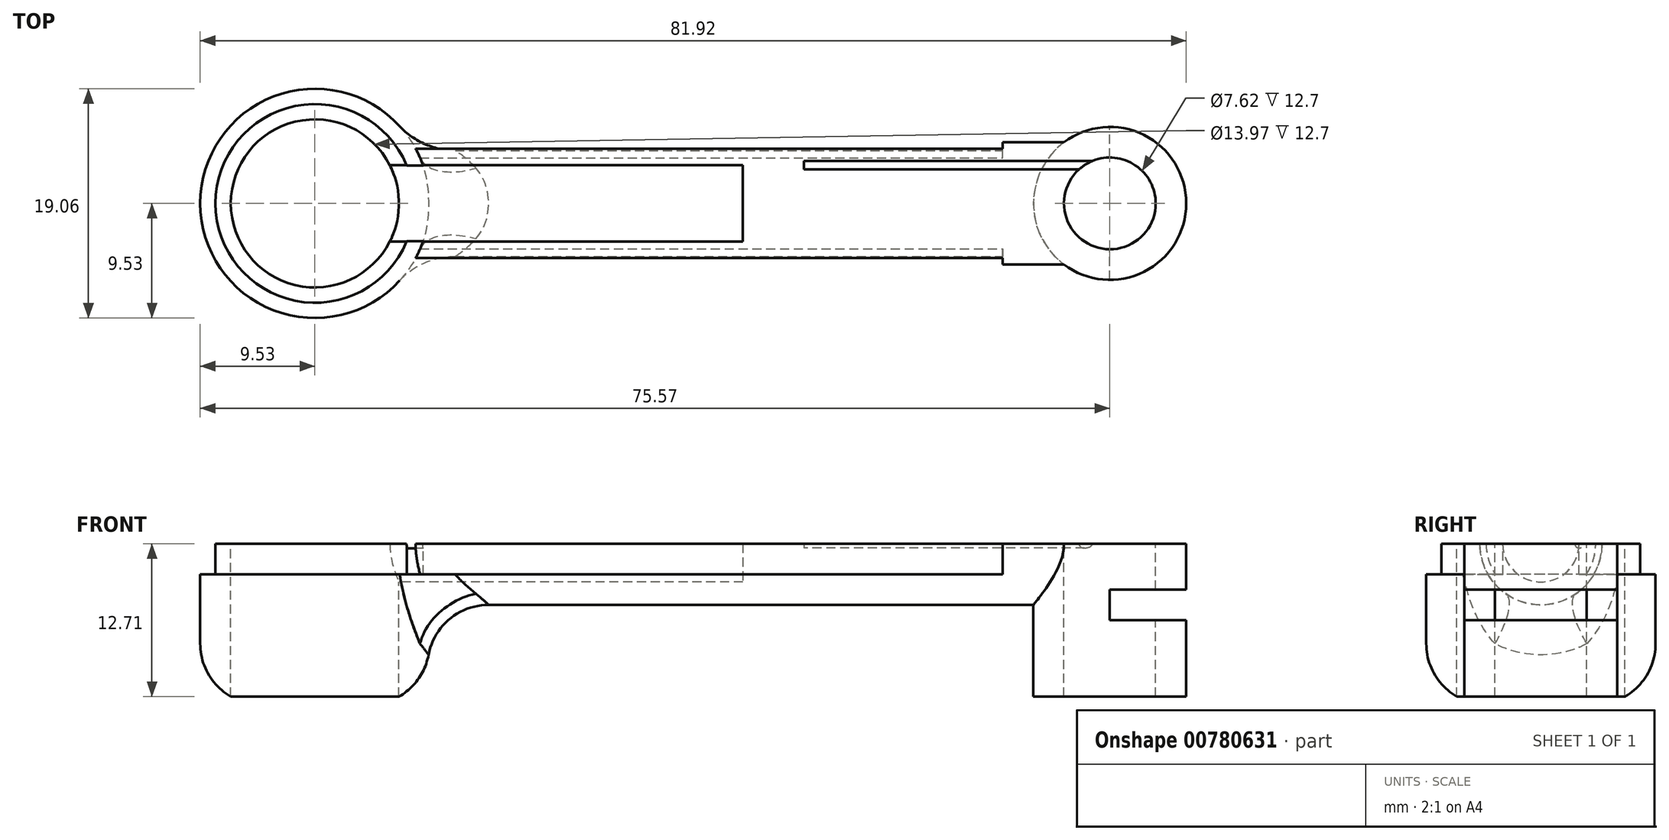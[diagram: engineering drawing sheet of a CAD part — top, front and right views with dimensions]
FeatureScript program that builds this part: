
annotation { "Feature Type Name" : "Feature", "Feature Type Description" : "" }
export const myFeature = defineFeature(function(context is Context, id is Id, definition is map)
    precondition{}
    {
        {
            var Q0;
            Q0=qCreatedBy(makeId("Top.planeOp"),FACE);
            var sketch = newSketch(context, id + "F0", { "sketchPlane" : qUnion([Q0])});
            skCircle(sketch, "E0", {"center": v(0, 0) * mm, "radius": 9.53 * mm});
            skSolve(sketch);
        }
        {
            var Q0;
            Q0=makeQuery(id+"F0.imprint","IMPRINT",FACE,{"disambiguationData":[TD([[makeQuery(id+"F0.imprint","IMPRINT",EDGE,{"derivedFrom":sQuery(id+"F0.wireOp",EDGE,"E0")}),1.0]])]});
            extrude(context, id + "F1", {"entities" : qUnion([Q0]), "depth" : 25.4 * mm, "offsetDistance" : 25.4 * mm});
        }
        {
            var Q0;
            Q0=makeQuery(id+"F1.opExtrude","CAP_FACE",FACE,{"disambiguationData":[OSD([sQuery(id+"F0.wireOp",EDGE,"E0")])],"isStart":false});
            var sketch = newSketch(context, id + "F2", { "sketchPlane" : qUnion([Q0])});
            skCircle(sketch, "E1", {"center": v(0, 0) * mm, "radius": 6.99 * mm});
            skSolve(sketch);
        }
        {
            var Q0;
            Q0=qCreatedBy(makeId("Right.planeOp"),FACE);
            var sketch = newSketch(context, id + "F3", { "sketchPlane" : qUnion([Q0])});
            skCircle(sketch, "E2", {"center": v(0, 15.88) * mm, "radius": 3.18 * mm});
            skSolve(sketch);
        }
        {
            var Q0;
            Q0=qSketchRegion(id+"F3",true);
            extrude(context, id + "F4", {"entities" : qUnion([Q0]), "operationType" : NewBodyOperationType.REMOVE, "depth" : 12.7 * mm, "offsetDistance" : 25.4 * mm});
        }
        {
            var Q0;
            Q0=qCreatedBy(makeId("Right.planeOp"),FACE);
            var sketch = newSketch(context, id + "F5", { "sketchPlane" : qUnion([Q0])});
            skLineSegment(sketch, "E3.top", {"start": v(9.53, 15.88) * mm, "end": v(-9.53, 15.88) * mm});
            skPoint(sketch, "E3.middle", {"position": v(0, 7.94) * mm});
            skLineSegment(sketch, "E4", {"start": v(-9.53, 15.88) * mm, "end": v(-9.53, 28.58) * mm});
            skLineSegment(sketch, "E5", {"start": v(9.53, 15.88) * mm, "end": v(9.53, 28.58) * mm});
            skLineSegment(sketch, "E6", {"start": v(-9.53, 28.58) * mm, "end": v(9.53, 28.58) * mm});
            skSolve(sketch);
        }
        {
            var Q0;
            Q0=qSketchRegion(id+"F5",true);
            extrude(context, id + "F6", {"entities" : qUnion([Q0]), "operationType" : NewBodyOperationType.REMOVE, "oppositeDirection" : true, "depth" : 25.4 * mm, "offsetDistance" : 25.4 * mm, "symmetric" : true});
        }
        {
            var Q0;
            Q0=qCreatedBy(makeId("Right.planeOp"),FACE);
            var sketch = newSketch(context, id + "F7", { "sketchPlane" : qUnion([Q0])});
            skArc(sketch, "E7", {"start": v(3.18, 15.88) * mm, "mid": v(0, 12.7) * mm, "end": v(-3.18, 15.88) * mm});
            skArc(sketch, "E8", {"start": v(-3.15, 18.42) * mm, "mid": v(-3.82, 17.22) * mm, "end": v(-4.05, 15.88) * mm});
            skArc(sketch, "E9", {"start": v(3.15, 18.42) * mm, "mid": v(3.82, 17.22) * mm, "end": v(4.05, 15.88) * mm});
            skLineSegment(sketch, "E10", {"start": v(-3.15, 18.42) * mm, "end": v(-4.4, 18.42) * mm});
            skLineSegment(sketch, "E11", {"start": v(3.15, 18.42) * mm, "end": v(4.4, 18.42) * mm});
            skLineSegment(sketch, "E12", {"start": v(-3.18, 15.88) * mm, "end": v(-4.05, 15.88) * mm});
            skLineSegment(sketch, "E13", {"start": v(3.18, 15.88) * mm, "end": v(4.05, 15.88) * mm});
            skArc(sketch, "E14", {"start": v(-4.4, 18.42) * mm, "mid": v(0, 10.8) * mm, "end": v(4.4, 18.42) * mm});
            skSolve(sketch);
        }
        {
            var Q0;
            Q0=qSketchRegion(id+"F7",true);
            var Q1;
            Q1=qConstructionFilter(qBodyType(qCreatedBy(id+"F7",EDGE),BodyType.WIRE),ConstructionObject.NO);
            extrude(context, id + "F8", {"entities" : qUnion([Q0]), "operationType" : NewBodyOperationType.ADD, "surfaceEntities" : qUnion([Q1]), "depth" : 38.1 * mm, "offsetDistance" : 25.4 * mm});
        }
        {
            var Q0;
            Q0=makeQuery(id+"F2.imprint","IMPRINT",FACE,{"disambiguationData":[TD([[makeQuery(id+"F2.imprint","IMPRINT",EDGE,{"derivedFrom":sQuery(id+"F2.wireOp",EDGE,"E1")}),1.0]])]});
            extrude(context, id + "F9", {"entities" : qUnion([Q0]), "operationType" : NewBodyOperationType.REMOVE, "oppositeDirection" : true, "depth" : 12.7 * mm, "offsetDistance" : 25.4 * mm});
        }
        {
            var Q0;
            Q0=makeQuery(id+"F8.opExtrude","CAP_FACE",FACE,{"disambiguationData":[OSD([sQuery(id+"F7.wireOp",EDGE,"E7"),sQuery(id+"F7.wireOp",EDGE,"E8"),sQuery(id+"F7.wireOp",EDGE,"E9"),sQuery(id+"F7.wireOp",EDGE,"E10"),sQuery(id+"F7.wireOp",EDGE,"E11"),sQuery(id+"F7.wireOp",EDGE,"E12"),sQuery(id+"F7.wireOp",EDGE,"E13"),sQuery(id+"F7.wireOp",EDGE,"E14")])],"isStart":false});
            var sketch = newSketch(context, id + "F10", { "sketchPlane" : qUnion([Q0])});
            skArc(sketch, "E15", {"start": v(-5.08, 15.88) * mm, "mid": v(0, 10.8) * mm, "end": v(5.08, 15.88) * mm});
            skArc(sketch, "E16", {"start": v(3.53, 15.88) * mm, "mid": v(3.17, 15.52) * mm, "end": v(2.82, 15.88) * mm});
            skLineSegment(sketch, "E17", {"start": v(-5.08, 15.88) * mm, "end": v(2.82, 15.88) * mm});
            skLineSegment(sketch, "E18", {"start": v(3.53, 15.88) * mm, "end": v(5.08, 15.88) * mm});
            skSolve(sketch);
        }
        {
            var Q0;
            Q0=qSketchRegion(id+"F10",true);
            extrude(context, id + "F11", {"entities" : qUnion([Q0]), "operationType" : NewBodyOperationType.ADD, "depth" : 24.13 * mm, "offsetDistance" : 25.4 * mm});
        }
        {
            var Q0;
            Q0=makeQuery(id+"F1.opExtrude","CAP_FACE",FACE,{"disambiguationData":[OSD([sQuery(id+"F0.wireOp",EDGE,"E0")])],"isStart":true});
            var sketch = newSketch(context, id + "F12", { "sketchPlane" : qUnion([Q0])});
            skCircle(sketch, "E19", {"center": v(-3.18, 3.18) * mm, "radius": 0.95 * mm});
            skCircle(sketch, "E20", {"center": v(3.18, 3.18) * mm, "radius": 0.95 * mm});
            skCircle(sketch, "E21", {"center": v(3.18, -3.18) * mm, "radius": 0.95 * mm});
            skCircle(sketch, "E22", {"center": v(-3.18, -3.18) * mm, "radius": 0.95 * mm});
            skSolve(sketch);
        }
        {
            var Q0;
            Q0=qSketchRegion(id+"F12",true);
            extrude(context, id + "F13", {"entities" : qUnion([Q0]), "operationType" : NewBodyOperationType.REMOVE, "oppositeDirection" : true, "depth" : 25.4 * mm, "offsetDistance" : 25.4 * mm});
        }
        {
            var Q0;
            Q0=makeQuery(id+"F1.opExtrude","CAP_FACE",FACE,{"disambiguationData":[OSD([sQuery(id+"F0.wireOp",EDGE,"E0")])],"isStart":true});
            var sketch = newSketch(context, id + "F14", { "sketchPlane" : qUnion([Q0])});
            skCircle(sketch, "E23", {"center": v(0, 0) * mm, "radius": 6.99 * mm});
            skSolve(sketch);
        }
        {
            var Q0;
            Q0=qSketchRegion(id+"F14",true);
            extrude(context, id + "F15", {"entities" : qUnion([Q0]), "operationType" : NewBodyOperationType.REMOVE, "oppositeDirection" : true, "depth" : 7.62 * mm, "offsetDistance" : 25.4 * mm});
        }
        {
            var Q0;
            Q0=makeQuery(id+"F9.boolean.opBoolean","SPLIT",FACE,{"disambiguationData":[TD([makeQuery(id+"F1.opExtrude","SWEPT_FACE",FACE,{"disambiguationData":[OSD([sQuery(id+"F0.wireOp",EDGE,"E0")])]})])],"derivedFrom":makeQuery(id+"F8.boolean.opBoolean","MERGE",FACE,{"derivedFrom":[makeQuery(id+"F6.boolean.opBoolean","COPY",FACE,{"derivedFrom":makeQuery(id+"F6.opExtrude","SWEPT_FACE",FACE,{"disambiguationData":[OSD([sQuery(id+"F5.wireOp",EDGE,"E3.top")])]})}),makeQuery(id+"F8.opExtrude","SWEPT_FACE",FACE,{"disambiguationData":[OSD([sQuery(id+"F7.wireOp",EDGE,"E12")])]}),makeQuery(id+"F8.opExtrude","SWEPT_FACE",FACE,{"disambiguationData":[OSD([sQuery(id+"F7.wireOp",EDGE,"E13")])]})]})});
            var sketch = newSketch(context, id + "F16", { "sketchPlane" : qUnion([Q0])});
            skCircle(sketch, "E24", {"center": v(0, 0) * mm, "radius": 6.99 * mm});
            skCircle(sketch, "E25", {"center": v(0, 0) * mm, "radius": 8.26 * mm});
            skSolve(sketch);
        }
        {
            var Q0;
            Q0=qSketchRegion(id+"F16",true);
            extrude(context, id + "F17", {"entities" : qUnion([Q0]), "operationType" : NewBodyOperationType.REMOVE, "depth" : 25.4 * mm, "offsetDistance" : 25.4 * mm});
        }
        {
            var Q0;
            Q0=makeQuery(id+"F8.opExtrude","SWEPT_FACE",FACE,{"disambiguationData":[OSD([sQuery(id+"F7.wireOp",EDGE,"E11")])]});
            var sketch = newSketch(context, id + "F18", { "sketchPlane" : qUnion([Q0])});
            skArc(sketch, "E26", {"start": v(7.63, 3.15) * mm, "mid": v(-8.25, 0) * mm, "end": v(7.63, -3.15) * mm});
            skArc(sketch, "E27", {"start": v(8.99, 3.15) * mm, "mid": v(-9.53, 0) * mm, "end": v(8.99, -3.15) * mm});
            skLineSegment(sketch, "E28", {"start": v(7.63, 3.15) * mm, "end": v(8.99, 3.15) * mm});
            skLineSegment(sketch, "E29", {"start": v(7.63, -3.15) * mm, "end": v(8.99, -3.15) * mm});
            skSolve(sketch);
        }
        {
            var Q0;
            Q0=qSketchRegion(id+"F18",true);
            extrude(context, id + "F19", {"entities" : qUnion([Q0]), "operationType" : NewBodyOperationType.REMOVE, "oppositeDirection" : true, "depth" : 5.08 * mm, "offsetDistance" : 25.4 * mm});
        }
        {
            var Q0;
            {var subQ0=sQuery(id+"F7.wireOp",EDGE,"E10");var subQ1=sQuery(id+"F7.wireOp",EDGE,"E8");var subQ2=sQuery(id+"F7.wireOp",EDGE,"E12");var subQ3=sQuery(id+"F7.wireOp",EDGE,"E13");var subQ4=sQuery(id+"F7.wireOp",EDGE,"E14");Q0=makeQuery(id+"F11.boolean.opBoolean","SPLIT",FACE,{"disambiguationData":[TD([makeQuery(id+"F8.opExtrude","SWEPT_FACE",FACE,{"disambiguationData":[OSD([subQ1])]})])],"derivedFrom":makeQuery(id+"F8.opExtrude","CAP_FACE",FACE,{"disambiguationData":[OSD([sQuery(id+"F7.wireOp",EDGE,"E7"),subQ1,sQuery(id+"F7.wireOp",EDGE,"E9"),subQ0,sQuery(id+"F7.wireOp",EDGE,"E11"),subQ2,subQ3,subQ4])],"isStart":false})});}
            var sketch = newSketch(context, id + "F20", { "sketchPlane" : qUnion([Q0])});
            skArc(sketch, "E30", {"start": v(-4.05, 15.88) * mm, "mid": v(0, 19.92) * mm, "end": v(4.05, 15.88) * mm});
            skLineSegment(sketch, "E31", {"start": v(-4.05, 15.88) * mm, "end": v(4.05, 15.88) * mm});
            skSolve(sketch);
        }
        {
            var Q0;
            Q0=qSketchRegion(id+"F20",true);
            extrude(context, id + "F21", {"entities" : qUnion([Q0]), "operationType" : NewBodyOperationType.REMOVE, "oppositeDirection" : true, "depth" : 63.5 * mm, "offsetDistance" : 25.4 * mm});
        }
        {
            var Q0;
            {var subQ0=sQuery(id+"F7.wireOp",EDGE,"E10");var subQ1=sQuery(id+"F7.wireOp",EDGE,"E8");var subQ2=sQuery(id+"F7.wireOp",EDGE,"E12");var subQ3=sQuery(id+"F7.wireOp",EDGE,"E13");var subQ4=sQuery(id+"F7.wireOp",EDGE,"E14");Q0=makeQuery(id+"F11.boolean.opBoolean","SPLIT",FACE,{"disambiguationData":[TD([makeQuery(id+"F8.opExtrude","SWEPT_FACE",FACE,{"disambiguationData":[OSD([subQ1])]})])],"derivedFrom":makeQuery(id+"F8.opExtrude","CAP_FACE",FACE,{"disambiguationData":[OSD([sQuery(id+"F7.wireOp",EDGE,"E7"),subQ1,sQuery(id+"F7.wireOp",EDGE,"E9"),subQ0,sQuery(id+"F7.wireOp",EDGE,"E11"),subQ2,subQ3,subQ4])],"isStart":false})});}
            var sketch = newSketch(context, id + "F22", { "sketchPlane" : qUnion([Q0])});
            skArc(sketch, "E32", {"start": v(-3.78, 13.34) * mm, "mid": v(-4.35, 14.55) * mm, "end": v(-4.55, 15.88) * mm});
            skLineSegment(sketch, "E33", {"start": v(-3.78, 13.34) * mm, "end": v(-4.4, 13.34) * mm});
            skArc(sketch, "E34", {"start": v(-3.15, 18.42) * mm, "mid": v(-3.82, 17.22) * mm, "end": v(-4.05, 15.88) * mm});
            skLineSegment(sketch, "E35", {"start": v(-4.55, 15.88) * mm, "end": v(-4.05, 15.88) * mm});
            skLineSegment(sketch, "E36", {"start": v(-3.15, 18.42) * mm, "end": v(-4.4, 18.42) * mm});
            skArc(sketch, "E37", {"start": v(-4.4, 13.34) * mm, "mid": v(-5.08, 15.88) * mm, "end": v(-4.4, 18.42) * mm});
            skSolve(sketch);
        }
        {
            var Q0;
            Q0=qSketchRegion(id+"F22",true);
            extrude(context, id + "F23", {"entities" : qUnion([Q0]), "operationType" : NewBodyOperationType.REMOVE, "oppositeDirection" : true, "depth" : 30.48 * mm, "offsetDistance" : 25.4 * mm});
        }
        {
            var Q0;
            {var subQ0=sQuery(id+"F7.wireOp",EDGE,"E11");var subQ1=sQuery(id+"F7.wireOp",EDGE,"E9");var subQ2=sQuery(id+"F7.wireOp",EDGE,"E12");var subQ3=sQuery(id+"F7.wireOp",EDGE,"E13");var subQ4=sQuery(id+"F7.wireOp",EDGE,"E14");Q0=makeQuery(id+"F11.boolean.opBoolean","SPLIT",FACE,{"disambiguationData":[TD([makeQuery(id+"F8.opExtrude","SWEPT_FACE",FACE,{"disambiguationData":[OSD([subQ1])]})])],"derivedFrom":makeQuery(id+"F8.opExtrude","CAP_FACE",FACE,{"disambiguationData":[OSD([sQuery(id+"F7.wireOp",EDGE,"E7"),sQuery(id+"F7.wireOp",EDGE,"E8"),subQ1,sQuery(id+"F7.wireOp",EDGE,"E10"),subQ0,subQ2,subQ3,subQ4])],"isStart":false})});}
            var sketch = newSketch(context, id + "F24", { "sketchPlane" : qUnion([Q0])});
            skArc(sketch, "E38", {"start": v(3.78, 13.34) * mm, "mid": v(4.35, 14.55) * mm, "end": v(4.55, 15.88) * mm});
            skLineSegment(sketch, "E39", {"start": v(4.55, 15.88) * mm, "end": v(4.05, 15.88) * mm});
            skArc(sketch, "E40", {"start": v(4.05, 15.88) * mm, "mid": v(3.82, 17.22) * mm, "end": v(3.15, 18.42) * mm});
            skLineSegment(sketch, "E41", {"start": v(3.15, 18.42) * mm, "end": v(4.4, 18.42) * mm});
            skLineSegment(sketch, "E42", {"start": v(3.78, 13.34) * mm, "end": v(4.4, 13.34) * mm});
            skArc(sketch, "E43", {"start": v(4.4, 13.34) * mm, "mid": v(5.08, 15.88) * mm, "end": v(4.4, 18.42) * mm});
            skSolve(sketch);
        }
        {
            var Q0;
            Q0=qSketchRegion(id+"F24",true);
            extrude(context, id + "F25", {"entities" : qUnion([Q0]), "operationType" : NewBodyOperationType.REMOVE, "oppositeDirection" : true, "depth" : 30.48 * mm, "offsetDistance" : 25.4 * mm});
        }
        {
            var Q0;
            Q0=qCreatedBy(makeId("Right.planeOp"),FACE);
            var sketch = newSketch(context, id + "F26", { "sketchPlane" : qUnion([Q0])});
            skLineSegment(sketch, "E44.bottom", {"start": v(-9.53, 0) * mm, "end": v(9.53, 0) * mm});
            skLineSegment(sketch, "E44.top", {"start": v(-9.53, 3.17) * mm, "end": v(9.53, 3.17) * mm});
            skLineSegment(sketch, "E44.left", {"start": v(-9.53, 0) * mm, "end": v(-9.53, 3.17) * mm});
            skLineSegment(sketch, "E44.right", {"start": v(9.53, 0) * mm, "end": v(9.53, 3.17) * mm});
            skSolve(sketch);
        }
        {
            var Q0;
            Q0=qSketchRegion(id+"F26",true);
            extrude(context, id + "F27", {"entities" : qUnion([Q0]), "operationType" : NewBodyOperationType.REMOVE, "oppositeDirection" : true, "depth" : 25.4 * mm, "offsetDistance" : 25.4 * mm, "symmetric" : true});
        }
        {
            var Q0;
            Q0=makeQuery(id+"F15.boolean.opBoolean","COPY",FACE,{"derivedFrom":makeQuery(id+"F15.opExtrude","CAP_FACE",FACE,{"disambiguationData":[OSD([sQuery(id+"F14.wireOp",EDGE,"E23")])],"isStart":false})});
            var sketch = newSketch(context, id + "F28", { "sketchPlane" : qUnion([Q0])});
            skCircle(sketch, "E45", {"center": v(0, 0) * mm, "radius": 6.99 * mm});
            skSolve(sketch);
        }
        {
            var Q0;
            Q0=qSketchRegion(id+"F28",true);
            extrude(context, id + "F29", {"entities" : qUnion([Q0]), "operationType" : NewBodyOperationType.REMOVE, "oppositeDirection" : true, "depth" : 25.4 * mm, "offsetDistance" : 25.4 * mm});
        }
        {
            var Q0;
            Q0=makeQuery(id+"F27.boolean.opBoolean","INTERSECT",EDGE,{"derivedFrom":[makeQuery(id+"F1.opExtrude","SWEPT_FACE",FACE,{"disambiguationData":[OSD([sQuery(id+"F0.wireOp",EDGE,"E0")])]}),makeQuery(id+"F27.opExtrude","SWEPT_FACE",FACE,{"disambiguationData":[OSD([sQuery(id+"F26.wireOp",EDGE,"E44.top")])]})]});
            fillet(context, id + "F30", {"entities" : qUnion([Q0]), "radius" : 5.08 * mm, "tangentPropagation" : true, "allowEdgeOverflow" : false});
        }
        {
            var Q0;
            Q0=makeQuery(id+"F19.boolean.opBoolean","SPLIT",EDGE,{"derivedFrom":makeQuery(id+"F8.boolean.opBoolean","INTERSECT",EDGE,{"derivedFrom":[makeQuery(id+"F1.opExtrude","SWEPT_FACE",FACE,{"disambiguationData":[OSD([sQuery(id+"F0.wireOp",EDGE,"E0")])]}),makeQuery(id+"F8.opExtrude","SWEPT_FACE",FACE,{"disambiguationData":[OSD([sQuery(id+"F7.wireOp",EDGE,"E14")])]})]})});
            fillet(context, id + "F31", {"entities" : qUnion([Q0]), "radius" : 5.08 * mm, "tangentPropagation" : true, "allowEdgeOverflow" : false});
        }
        {
            var Q0;
            {var subQ0=sQuery(id+"F7.wireOp",EDGE,"E9");var subQ1=makeQuery(id+"F8.opExtrude","SWEPT_FACE",FACE,{"disambiguationData":[OSD([subQ0])]});var subQ2=sQuery(id+"F10.wireOp",EDGE,"aL0u9GlF-6Q7s-W1V7-4wS0-8lCQG8VcdnJv");var subQ3=sQuery(id+"F10.wireOp",EDGE,"2Tc0jqr0-cNR8-OvJQ-WwAY-mDO75ud9QsQn");var subQ7=sQuery(id+"F7.wireOp",EDGE,"E13");var subQ8=sQuery(id+"F7.wireOp",EDGE,"E12");var subQ9=sQuery(id+"F7.wireOp",EDGE,"E8");var subQ16=makeQuery(id+"F8.boolean.opBoolean","MERGE",FACE,{"derivedFrom":[makeQuery(id+"F6.boolean.opBoolean","COPY",FACE,{"derivedFrom":makeQuery(id+"F6.opExtrude","SWEPT_FACE",FACE,{"disambiguationData":[OSD([sQuery(id+"F5.wireOp",EDGE,"E3.top")])]})}),makeQuery(id+"F8.opExtrude","SWEPT_FACE",FACE,{"disambiguationData":[OSD([subQ8])]}),makeQuery(id+"F8.opExtrude","SWEPT_FACE",FACE,{"disambiguationData":[OSD([subQ7])]})]});Q0=makeQuery(id+"F25.boolean.opBoolean","MERGE",FACE,{"derivedFrom":[makeQuery(id+"F19.boolean.opBoolean","SPLIT",FACE,{"disambiguationData":[TD([subQ1])],"derivedFrom":makeQuery(id+"F17.boolean.opBoolean","MERGE",FACE,{"derivedFrom":[makeQuery(id+"F9.boolean.opBoolean","SPLIT",FACE,{"disambiguationData":[TD([makeQuery(id+"F1.opExtrude","SWEPT_FACE",FACE,{"disambiguationData":[OSD([sQuery(id+"F0.wireOp",EDGE,"E0")])]})])],"derivedFrom":subQ16}),makeQuery(id+"F11.boolean.opBoolean","MERGE",FACE,{"derivedFrom":[makeQuery(id+"F9.boolean.opBoolean","SPLIT",FACE,{"disambiguationData":[TD([makeQuery(id+"F8.opExtrude","SWEPT_FACE",FACE,{"disambiguationData":[OSD([subQ9])]})])],"derivedFrom":subQ16}),makeQuery(id+"F11.opExtrude","SWEPT_FACE",FACE,{"disambiguationData":[OSD([subQ2])]})]}),makeQuery(id+"F11.boolean.opBoolean","MERGE",FACE,{"derivedFrom":[makeQuery(id+"F9.boolean.opBoolean","SPLIT",FACE,{"disambiguationData":[TD([subQ1])],"derivedFrom":subQ16}),makeQuery(id+"F11.opExtrude","SWEPT_FACE",FACE,{"disambiguationData":[OSD([subQ3])]})]}),makeQuery(id+"F17.opExtrude","CAP_FACE",FACE,{"disambiguationData":[OSD([sQuery(id+"F16.wireOp",EDGE,"E24"),sQuery(id+"F16.wireOp",EDGE,"E25")])],"isStart":true})]})}),makeQuery(id+"F25.opExtrude","SWEPT_FACE",FACE,{"disambiguationData":[OSD([sQuery(id+"F24.wireOp",EDGE,"E39")])]})]});}
            var sketch = newSketch(context, id + "F32", { "sketchPlane" : qUnion([Q0])});
            skCircle(sketch, "E46", {"center": v(66.04, 0) * mm, "radius": 3.81 * mm});
            skCircle(sketch, "E47", {"center": v(66.04, 0) * mm, "radius": 6.35 * mm});
            skSolve(sketch);
        }
        {
            var Q0;
            Q0=qSketchRegion(id+"F32",true);
            extrude(context, id + "F33", {"entities" : qUnion([Q0]), "operationType" : NewBodyOperationType.ADD, "oppositeDirection" : true, "depth" : 12.7 * mm, "offsetDistance" : 25.4 * mm});
        }
        {
            var Q0;
            Q0=makeQuery(id+"F11.opExtrude","CAP_FACE",FACE,{"disambiguationData":[OSD([sQuery(id+"F10.wireOp",EDGE,"E15"),sQuery(id+"F10.wireOp",EDGE,"00xkIltH-ur7c-vDCf-NMd2-okXEgH0ywGPR"),sQuery(id+"F10.wireOp",EDGE,"2Tc0jqr0-cNR8-OvJQ-WwAY-mDO75ud9QsQn"),sQuery(id+"F10.wireOp",EDGE,"aL0u9GlF-6Q7s-W1V7-4wS0-8lCQG8VcdnJv")])],"isStart":true});
            var sketch = newSketch(context, id + "F34", { "sketchPlane" : qUnion([Q0])});
            skArc(sketch, "E48", {"start": v(-3.18, 15.88) * mm, "mid": v(0, 12.7) * mm, "end": v(3.18, 15.88) * mm});
            skLineSegment(sketch, "E49", {"start": v(-3.18, 15.88) * mm, "end": v(3.18, 15.88) * mm});
            skSolve(sketch);
        }
        {
            var Q0;
            Q0=qSketchRegion(id+"F34",true);
            extrude(context, id + "F35", {"entities" : qUnion([Q0]), "operationType" : NewBodyOperationType.ADD, "depth" : 2.54 * mm, "offsetDistance" : 25.4 * mm});
        }
        {
            var Q0;
            {var subQ0=sQuery(id+"F7.wireOp",EDGE,"E7");var subQ1=sQuery(id+"F7.wireOp",EDGE,"E12");var subQ4=sQuery(id+"F7.wireOp",EDGE,"E13");Q0=makeQuery(id+"F35.boolean.opBoolean","MERGE",FACE,{"derivedFrom":[makeQuery(id+"F11.boolean.opBoolean","SPLIT",FACE,{"disambiguationData":[TD([makeQuery(id+"F4.boolean.opBoolean","COPY",FACE,{"derivedFrom":makeQuery(id+"F4.opExtrude","SWEPT_FACE",FACE,{"disambiguationData":[OSD([sQuery(id+"F3.wireOp",EDGE,"E2")])]})})])],"derivedFrom":makeQuery(id+"F8.opExtrude","CAP_FACE",FACE,{"disambiguationData":[OSD([subQ0,sQuery(id+"F7.wireOp",EDGE,"E8"),sQuery(id+"F7.wireOp",EDGE,"E9"),sQuery(id+"F7.wireOp",EDGE,"E10"),sQuery(id+"F7.wireOp",EDGE,"E11"),subQ1,subQ4,sQuery(id+"F7.wireOp",EDGE,"E14")])],"isStart":false})}),makeQuery(id+"F35.opExtrude","CAP_FACE",FACE,{"disambiguationData":[OSD([sQuery(id+"F34.wireOp",EDGE,"E48"),sQuery(id+"F34.wireOp",EDGE,"E49")])],"isStart":true})]});}
            extrude(context, id + "F36", {"entities" : qUnion([Q0]), "operationType" : NewBodyOperationType.REMOVE, "depth" : 27.94 * mm, "offsetDistance" : 25.4 * mm});
        }
        {
            var Q0;
            Q0=makeQuery(id+"F23.boolean.opBoolean","COPY",FACE,{"derivedFrom":makeQuery(id+"F23.opExtrude","CAP_FACE",FACE,{"disambiguationData":[OSD([sQuery(id+"F22.wireOp",EDGE,"E32"),sQuery(id+"F22.wireOp",EDGE,"E33"),sQuery(id+"F22.wireOp",EDGE,"E34"),sQuery(id+"F22.wireOp",EDGE,"E35"),sQuery(id+"F22.wireOp",EDGE,"E36"),sQuery(id+"F22.wireOp",EDGE,"E37")])],"isStart":true})});
            extrude(context, id + "F37", {"entities" : qUnion([Q0]), "operationType" : NewBodyOperationType.REMOVE, "oppositeDirection" : true, "depth" : 19.05 * mm, "offsetDistance" : 25.4 * mm});
        }
        {
            var Q0;
            Q0=makeQuery(id+"F25.boolean.opBoolean","COPY",FACE,{"derivedFrom":makeQuery(id+"F25.opExtrude","CAP_FACE",FACE,{"disambiguationData":[OSD([sQuery(id+"F24.wireOp",EDGE,"E38"),sQuery(id+"F24.wireOp",EDGE,"E39"),sQuery(id+"F24.wireOp",EDGE,"E40"),sQuery(id+"F24.wireOp",EDGE,"E41"),sQuery(id+"F24.wireOp",EDGE,"E42"),sQuery(id+"F24.wireOp",EDGE,"E43")])],"isStart":true})});
            extrude(context, id + "F38", {"entities" : qUnion([Q0]), "operationType" : NewBodyOperationType.REMOVE, "oppositeDirection" : true, "depth" : 19.05 * mm, "offsetDistance" : 25.4 * mm});
        }
        {
            var Q0;
            {var subQ0=sQuery(id+"F7.wireOp",EDGE,"E9");var subQ1=makeQuery(id+"F8.opExtrude","SWEPT_FACE",FACE,{"disambiguationData":[OSD([subQ0])]});var subQ2=sQuery(id+"F10.wireOp",EDGE,"Va9SlXQ7-r9gY-A2W4-oZNz-J4n8oxZGjyvQ");var subQ3=sQuery(id+"F10.wireOp",EDGE,"Rd6kEXFY-NNdW-kPoJ-Zn7l-Uw842lO794nO");var subQ8=sQuery(id+"F7.wireOp",EDGE,"E13");var subQ9=sQuery(id+"F7.wireOp",EDGE,"E12");var subQ10=sQuery(id+"F7.wireOp",EDGE,"E8");var subQ20=makeQuery(id+"F8.boolean.opBoolean","MERGE",FACE,{"derivedFrom":[makeQuery(id+"F6.boolean.opBoolean","COPY",FACE,{"derivedFrom":makeQuery(id+"F6.opExtrude","SWEPT_FACE",FACE,{"disambiguationData":[OSD([sQuery(id+"F5.wireOp",EDGE,"E3.top")])]})}),makeQuery(id+"F8.opExtrude","SWEPT_FACE",FACE,{"disambiguationData":[OSD([subQ9])]}),makeQuery(id+"F8.opExtrude","SWEPT_FACE",FACE,{"disambiguationData":[OSD([subQ8])]})]});var subQ21=makeQuery(id+"F8.opExtrude","SWEPT_FACE",FACE,{"disambiguationData":[OSD([subQ10])]});var subQ22=makeQuery(id+"F17.boolean.opBoolean","MERGE",FACE,{"derivedFrom":[makeQuery(id+"F9.boolean.opBoolean","SPLIT",FACE,{"disambiguationData":[TD([makeQuery(id+"F1.opExtrude","SWEPT_FACE",FACE,{"disambiguationData":[OSD([sQuery(id+"F0.wireOp",EDGE,"E0")])]})])],"derivedFrom":subQ20}),makeQuery(id+"F11.boolean.opBoolean","MERGE",FACE,{"derivedFrom":[makeQuery(id+"F9.boolean.opBoolean","SPLIT",FACE,{"disambiguationData":[TD([subQ21])],"derivedFrom":subQ20}),makeQuery(id+"F11.opExtrude","SWEPT_FACE",FACE,{"disambiguationData":[OSD([subQ2])]})]}),makeQuery(id+"F11.boolean.opBoolean","MERGE",FACE,{"derivedFrom":[makeQuery(id+"F9.boolean.opBoolean","SPLIT",FACE,{"disambiguationData":[TD([subQ1])],"derivedFrom":subQ20}),makeQuery(id+"F11.opExtrude","SWEPT_FACE",FACE,{"disambiguationData":[OSD([subQ3])]})]}),makeQuery(id+"F17.opExtrude","CAP_FACE",FACE,{"disambiguationData":[OSD([sQuery(id+"F16.wireOp",EDGE,"E24"),sQuery(id+"F16.wireOp",EDGE,"E25")])],"isStart":true})]});Q0=makeQuery(id+"F35.boolean.opBoolean","MERGE",FACE,{"derivedFrom":[makeQuery(id+"F33.boolean.opBoolean","MERGE",FACE,{"derivedFrom":[makeQuery(id+"F23.boolean.opBoolean","MERGE",FACE,{"derivedFrom":[makeQuery(id+"F19.boolean.opBoolean","SPLIT",FACE,{"disambiguationData":[TD([subQ21])],"derivedFrom":subQ22}),makeQuery(id+"F23.opExtrude","SWEPT_FACE",FACE,{"disambiguationData":[OSD([sQuery(id+"F22.wireOp",EDGE,"E35")])]})]}),makeQuery(id+"F25.boolean.opBoolean","MERGE",FACE,{"derivedFrom":[makeQuery(id+"F19.boolean.opBoolean","SPLIT",FACE,{"disambiguationData":[TD([subQ1])],"derivedFrom":subQ22}),makeQuery(id+"F25.opExtrude","SWEPT_FACE",FACE,{"disambiguationData":[OSD([sQuery(id+"F24.wireOp",EDGE,"E39")])]})]}),makeQuery(id+"F33.opExtrude","CAP_FACE",FACE,{"disambiguationData":[OSD([sQuery(id+"F32.wireOp",EDGE,"E46"),sQuery(id+"F32.wireOp",EDGE,"E47")])],"isStart":true})]}),makeQuery(id+"F35.opExtrude","SWEPT_FACE",FACE,{"disambiguationData":[OSD([sQuery(id+"F34.wireOp",EDGE,"E49")])]})]});}
            var sketch = newSketch(context, id + "F39", { "sketchPlane" : qUnion([Q0])});
            skArc(sketch, "E50", {"start": v(66.04, 6.35) * mm, "mid": v(72.39, 0) * mm, "end": v(66.04, -6.35) * mm});
            skLineSegment(sketch, "E51", {"start": v(66.04, 6.35) * mm, "end": v(66.04, -6.35) * mm});
            skSolve(sketch);
        }
        {
            var Q0;
            Q0=qSketchRegion(id+"F39",true);
            extrude(context, id + "F40", {"entities" : qUnion([Q0]), "operationType" : NewBodyOperationType.REMOVE, "oppositeDirection" : true, "depth" : 6.35 * mm, "offsetDistance" : 25.4 * mm});
        }
        {
            var Q0;
            {var subQ0=sQuery(id+"F7.wireOp",EDGE,"E9");var subQ1=makeQuery(id+"F8.opExtrude","SWEPT_FACE",FACE,{"disambiguationData":[OSD([subQ0])]});var subQ2=sQuery(id+"F10.wireOp",EDGE,"Va9SlXQ7-r9gY-A2W4-oZNz-J4n8oxZGjyvQ");var subQ3=sQuery(id+"F10.wireOp",EDGE,"Rd6kEXFY-NNdW-kPoJ-Zn7l-Uw842lO794nO");var subQ8=sQuery(id+"F7.wireOp",EDGE,"E13");var subQ9=sQuery(id+"F7.wireOp",EDGE,"E12");var subQ10=sQuery(id+"F7.wireOp",EDGE,"E8");var subQ20=makeQuery(id+"F8.boolean.opBoolean","MERGE",FACE,{"derivedFrom":[makeQuery(id+"F6.boolean.opBoolean","COPY",FACE,{"derivedFrom":makeQuery(id+"F6.opExtrude","SWEPT_FACE",FACE,{"disambiguationData":[OSD([sQuery(id+"F5.wireOp",EDGE,"E3.top")])]})}),makeQuery(id+"F8.opExtrude","SWEPT_FACE",FACE,{"disambiguationData":[OSD([subQ9])]}),makeQuery(id+"F8.opExtrude","SWEPT_FACE",FACE,{"disambiguationData":[OSD([subQ8])]})]});var subQ21=makeQuery(id+"F8.opExtrude","SWEPT_FACE",FACE,{"disambiguationData":[OSD([subQ10])]});var subQ22=makeQuery(id+"F17.boolean.opBoolean","MERGE",FACE,{"derivedFrom":[makeQuery(id+"F9.boolean.opBoolean","SPLIT",FACE,{"disambiguationData":[TD([makeQuery(id+"F1.opExtrude","SWEPT_FACE",FACE,{"disambiguationData":[OSD([sQuery(id+"F0.wireOp",EDGE,"E0")])]})])],"derivedFrom":subQ20}),makeQuery(id+"F11.boolean.opBoolean","MERGE",FACE,{"derivedFrom":[makeQuery(id+"F9.boolean.opBoolean","SPLIT",FACE,{"disambiguationData":[TD([subQ21])],"derivedFrom":subQ20}),makeQuery(id+"F11.opExtrude","SWEPT_FACE",FACE,{"disambiguationData":[OSD([subQ2])]})]}),makeQuery(id+"F11.boolean.opBoolean","MERGE",FACE,{"derivedFrom":[makeQuery(id+"F9.boolean.opBoolean","SPLIT",FACE,{"disambiguationData":[TD([subQ1])],"derivedFrom":subQ20}),makeQuery(id+"F11.opExtrude","SWEPT_FACE",FACE,{"disambiguationData":[OSD([subQ3])]})]}),makeQuery(id+"F17.opExtrude","CAP_FACE",FACE,{"disambiguationData":[OSD([sQuery(id+"F16.wireOp",EDGE,"E24"),sQuery(id+"F16.wireOp",EDGE,"E25")])],"isStart":true})]});Q0=makeQuery(id+"F35.boolean.opBoolean","MERGE",FACE,{"derivedFrom":[makeQuery(id+"F33.boolean.opBoolean","MERGE",FACE,{"derivedFrom":[makeQuery(id+"F23.boolean.opBoolean","MERGE",FACE,{"derivedFrom":[makeQuery(id+"F19.boolean.opBoolean","SPLIT",FACE,{"disambiguationData":[TD([subQ21])],"derivedFrom":subQ22}),makeQuery(id+"F23.opExtrude","SWEPT_FACE",FACE,{"disambiguationData":[OSD([sQuery(id+"F22.wireOp",EDGE,"E35")])]})]}),makeQuery(id+"F25.boolean.opBoolean","MERGE",FACE,{"derivedFrom":[makeQuery(id+"F19.boolean.opBoolean","SPLIT",FACE,{"disambiguationData":[TD([subQ1])],"derivedFrom":subQ22}),makeQuery(id+"F25.opExtrude","SWEPT_FACE",FACE,{"disambiguationData":[OSD([sQuery(id+"F24.wireOp",EDGE,"E39")])]})]}),makeQuery(id+"F33.opExtrude","CAP_FACE",FACE,{"disambiguationData":[OSD([sQuery(id+"F32.wireOp",EDGE,"E46"),sQuery(id+"F32.wireOp",EDGE,"E47")])],"isStart":true})]}),makeQuery(id+"F35.opExtrude","SWEPT_FACE",FACE,{"disambiguationData":[OSD([sQuery(id+"F34.wireOp",EDGE,"E49")])]})]});}
            var sketch = newSketch(context, id + "F41", { "sketchPlane" : qUnion([Q0])});
            skArc(sketch, "E52", {"start": v(64.58, 6.18) * mm, "mid": v(72.39, -0.02) * mm, "end": v(64.53, -6.17) * mm});
            skArc(sketch, "E53", {"start": v(65.21, 3.72) * mm, "mid": v(69.85, 0.08) * mm, "end": v(65.36, -3.75) * mm});
            skLineSegment(sketch, "E54", {"start": v(65.21, 3.72) * mm, "end": v(64.58, 6.18) * mm});
            skLineSegment(sketch, "E55", {"start": v(65.36, -3.75) * mm, "end": v(64.53, -6.17) * mm});
            skSolve(sketch);
        }
        {
            var Q0;
            Q0=qSketchRegion(id+"F41",true);
            extrude(context, id + "F42", {"entities" : qUnion([Q0]), "operationType" : NewBodyOperationType.ADD, "oppositeDirection" : true, "depth" : 3.8 * mm, "offsetDistance" : 25.4 * mm});
        }
        {
            var Q0;
            {var subQ0=sQuery(id+"F7.wireOp",EDGE,"E7");var subQ1=sQuery(id+"F7.wireOp",EDGE,"E12");var subQ4=sQuery(id+"F7.wireOp",EDGE,"E13");Q0=makeQuery(id+"F35.boolean.opBoolean","MERGE",FACE,{"derivedFrom":[makeQuery(id+"F11.boolean.opBoolean","SPLIT",FACE,{"disambiguationData":[TD([makeQuery(id+"F4.boolean.opBoolean","COPY",FACE,{"derivedFrom":makeQuery(id+"F4.opExtrude","SWEPT_FACE",FACE,{"disambiguationData":[OSD([sQuery(id+"F3.wireOp",EDGE,"E2")])]})})])],"derivedFrom":makeQuery(id+"F8.opExtrude","CAP_FACE",FACE,{"disambiguationData":[OSD([subQ0,sQuery(id+"F7.wireOp",EDGE,"E8"),sQuery(id+"F7.wireOp",EDGE,"E9"),sQuery(id+"F7.wireOp",EDGE,"E10"),sQuery(id+"F7.wireOp",EDGE,"E11"),subQ1,subQ4,sQuery(id+"F7.wireOp",EDGE,"E14")])],"isStart":false})}),makeQuery(id+"F35.opExtrude","CAP_FACE",FACE,{"disambiguationData":[OSD([sQuery(id+"F34.wireOp",EDGE,"E48"),sQuery(id+"F34.wireOp",EDGE,"E49")])],"isStart":true})]});}
            extrude(context, id + "F43", {"entities" : qUnion([Q0]), "operationType" : NewBodyOperationType.ADD, "depth" : 2.54 * mm, "offsetDistance" : 25.4 * mm});
        }
    });
